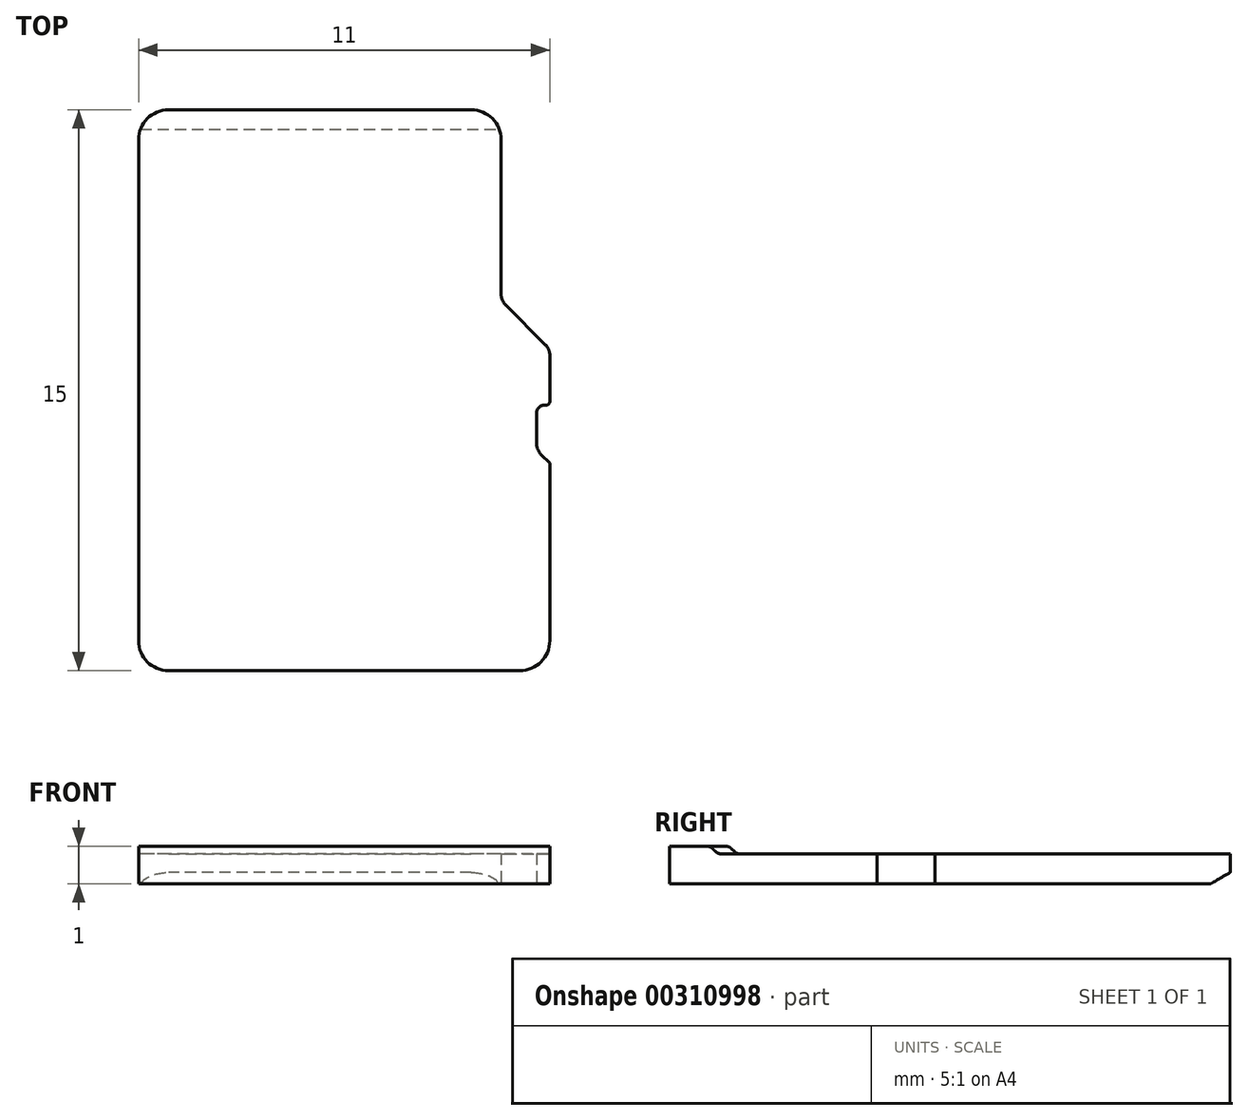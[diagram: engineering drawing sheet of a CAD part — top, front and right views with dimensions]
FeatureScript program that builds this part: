
annotation { "Feature Type Name" : "Feature", "Feature Type Description" : "" }
export const myFeature = defineFeature(function(context is Context, id is Id, definition is map)
    precondition{}
    {
        {
            var Q0;
            Q0=qCreatedBy(makeId("Top.planeOp"),FACE);
            var sketch = newSketch(context, id + "F0", { "sketchPlane" : qUnion([Q0])});
            skLineSegment(sketch, "E0.bottom", {"start": v(-0.8, 0) * mm, "end": v(-10.2, 0) * mm});
            skLineSegment(sketch, "E0.top", {"start": v(0, 15) * mm, "end": v(-11, 15) * mm, "construction": true});
            skLineSegment(sketch, "E0.left", {"start": v(0, 0) * mm, "end": v(0, 5.55) * mm, "construction": true});
            skLineSegment(sketch, "E0.right", {"start": v(-11, 0.8) * mm, "end": v(-11, 14.2) * mm});
            skLineSegment(sketch, "E1", {"start": v(-1.3, 14.2) * mm, "end": v(-1.3, 10.07) * mm});
            skLineSegment(sketch, "E2", {"start": v(-1.18, 9.78) * mm, "end": v(-0.12, 8.72) * mm});
            skLineSegment(sketch, "E3", {"start": v(-10.2, 15) * mm, "end": v(-2.1, 15) * mm});
            skLineSegment(sketch, "E4", {"start": v(0, 8.43) * mm, "end": v(0, 7.2) * mm});
            skPoint(sketch, "E5.visualSharp", {"position": v(-1.3, 15) * mm});
            skArc(sketch, "E5.filletArc", {"start": v(-1.3, 14.2) * mm, "mid": v(-1.53, 14.77) * mm, "end": v(-2.1, 15) * mm});
            skPoint(sketch, "E6.visualSharp", {"position": v(-11, 15) * mm});
            skArc(sketch, "E6.filletArc", {"start": v(-10.2, 15) * mm, "mid": v(-10.77, 14.77) * mm, "end": v(-11, 14.2) * mm});
            skPoint(sketch, "E7.visualSharp", {"position": v(-11, 0) * mm});
            skArc(sketch, "E7.filletArc", {"start": v(-11, 0.8) * mm, "mid": v(-10.77, 0.23) * mm, "end": v(-10.2, 0) * mm});
            skPoint(sketch, "E8.visualSharp", {"position": v(0, 0) * mm});
            skArc(sketch, "E8.filletArc", {"start": v(-0.8, 0) * mm, "mid": v(-0.23, 0.23) * mm, "end": v(0, 0.8) * mm});
            skPoint(sketch, "E9.visualSharp", {"position": v(-1.3, 9.9) * mm});
            skArc(sketch, "E9.filletArc", {"start": v(-1.3, 10.07) * mm, "mid": v(-1.27, 9.91) * mm, "end": v(-1.18, 9.78) * mm});
            skArc(sketch, "E10", {"start": v(0, 1.33) * mm, "mid": v(-5.5, 1.84) * mm, "end": v(-11, 1.33) * mm});
            skArc(sketch, "E11", {"start": v(0, 1) * mm, "mid": v(-5.5, 1.5) * mm, "end": v(-11, 1) * mm});
            skLineSegment(sketch, "E12", {"start": v(-0.1, 7.1) * mm, "end": v(-0.15, 7.1) * mm});
            skLineSegment(sketch, "E13", {"start": v(-0.35, 6.9) * mm, "end": v(-0.35, 6.07) * mm});
            skLineSegment(sketch, "E14", {"start": v(-0.23, 5.78) * mm, "end": v(0, 5.55) * mm});
            skLineSegment(sketch, "E15.trimOffspring", {"start": v(0, 7.1) * mm, "end": v(0, 15) * mm, "construction": true});
            skLineSegment(sketch, "E16.trimOffspring", {"start": v(0, 5.55) * mm, "end": v(0, 0.8) * mm});
            skPoint(sketch, "E17.visualSharp", {"position": v(-0.35, 5.9) * mm});
            skArc(sketch, "E17.filletArc", {"start": v(-0.35, 6.07) * mm, "mid": v(-0.32, 5.91) * mm, "end": v(-0.23, 5.78) * mm});
            skPoint(sketch, "E18.visualSharp", {"position": v(-0.35, 7.1) * mm});
            skArc(sketch, "E18.filletArc", {"start": v(-0.15, 7.1) * mm, "mid": v(-0.3, 7.04) * mm, "end": v(-0.35, 6.9) * mm});
            skPoint(sketch, "E19.visualSharp", {"position": v(0, 7.1) * mm});
            skArc(sketch, "E19.filletArc", {"start": v(-0.1, 7.1) * mm, "mid": v(-0.03, 7.13) * mm, "end": v(0, 7.2) * mm});
            skPoint(sketch, "E20.visualSharp", {"position": v(0, 8.6) * mm});
            skArc(sketch, "E20.filletArc", {"start": v(0, 8.43) * mm, "mid": v(-0.03, 8.59) * mm, "end": v(-0.12, 8.72) * mm});
            skSolve(sketch);
        }
        {
            var Q0;
            Q0=qSketchRegion(id+"F0",true);
            extrude(context, id + "F1", {"entities" : qUnion([Q0]), "depth" : .8 * mm});
        }
        {
            var Q0;
            Q0=makeQuery(id+"F0.imprint","IMPRINT",FACE,{"disambiguationData":[TD([[makeQuery(id+"F0.imprint","IMPRINT",EDGE,{"derivedFrom":sQuery(id+"F0.wireOp",EDGE,"E0.bottom")}),-1.0]])]});
            extrude(context, id + "F2", {"entities" : qUnion([Q0]), "operationType" : NewBodyOperationType.ADD, "depth" : 1 * mm});
        }
        {
            var Q0;
            Q0=makeQuery(id+"F2.boolean.opBoolean","INTERSECT",EDGE,{"derivedFrom":[makeQuery(id+"F1.opExtrude","CAP_FACE",FACE,{"disambiguationData":[OSD([sQuery(id+"F0.wireOp",EDGE,"E0.bottom"),sQuery(id+"F0.wireOp",EDGE,"E0.right"),sQuery(id+"F0.wireOp",EDGE,"E1"),sQuery(id+"F0.wireOp",EDGE,"E2"),sQuery(id+"F0.wireOp",EDGE,"E3"),sQuery(id+"F0.wireOp",EDGE,"E4"),sQuery(id+"F0.wireOp",EDGE,"E5.filletArc"),sQuery(id+"F0.wireOp",EDGE,"E6.filletArc"),sQuery(id+"F0.wireOp",EDGE,"E7.filletArc"),sQuery(id+"F0.wireOp",EDGE,"E8.filletArc"),sQuery(id+"F0.wireOp",EDGE,"E9.filletArc"),sQuery(id+"F0.wireOp",EDGE,"E12"),sQuery(id+"F0.wireOp",EDGE,"E13"),sQuery(id+"F0.wireOp",EDGE,"E14"),sQuery(id+"F0.wireOp",EDGE,"E16.trimOffspring"),sQuery(id+"F0.wireOp",EDGE,"E17.filletArc"),sQuery(id+"F0.wireOp",EDGE,"E18.filletArc"),sQuery(id+"F0.wireOp",EDGE,"E19.filletArc"),sQuery(id+"F0.wireOp",EDGE,"E20.filletArc")])],"isStart":false}),makeQuery(id+"F2.opExtrude","SWEPT_FACE",FACE,{"disambiguationData":[OSD([sQuery(id+"F0.wireOp",EDGE,"E11")])]})]});
            chamfer(context, id + "F3", {"entities" : qUnion([Q0]), "width" : .3 * mm, "tangentPropagation" : true});
        }
        {
            var Q0;
            {var subQ0=makeQuery(id+"F1.opExtrude","CAP_FACE",FACE,{"disambiguationData":[OSD([sQuery(id+"F0.wireOp",EDGE,"E0.bottom"),sQuery(id+"F0.wireOp",EDGE,"E0.right"),sQuery(id+"F0.wireOp",EDGE,"E1"),sQuery(id+"F0.wireOp",EDGE,"E2"),sQuery(id+"F0.wireOp",EDGE,"E3"),sQuery(id+"F0.wireOp",EDGE,"E4"),sQuery(id+"F0.wireOp",EDGE,"E5.filletArc"),sQuery(id+"F0.wireOp",EDGE,"E6.filletArc"),sQuery(id+"F0.wireOp",EDGE,"E7.filletArc"),sQuery(id+"F0.wireOp",EDGE,"E8.filletArc"),sQuery(id+"F0.wireOp",EDGE,"E9.filletArc"),sQuery(id+"F0.wireOp",EDGE,"E12"),sQuery(id+"F0.wireOp",EDGE,"E13"),sQuery(id+"F0.wireOp",EDGE,"E14"),sQuery(id+"F0.wireOp",EDGE,"E16.trimOffspring"),sQuery(id+"F0.wireOp",EDGE,"E17.filletArc"),sQuery(id+"F0.wireOp",EDGE,"E18.filletArc"),sQuery(id+"F0.wireOp",EDGE,"E19.filletArc"),sQuery(id+"F0.wireOp",EDGE,"E20.filletArc")])],"isStart":false});Q0=makeQuery(id+"F3.opChamfer","BLEND_EDGE",EDGE,{"blendedFrom":[makeQuery(id+"F2.boolean.opBoolean","INTERSECT",EDGE,{"derivedFrom":[subQ0,makeQuery(id+"F2.opExtrude","SWEPT_FACE",FACE,{"disambiguationData":[OSD([sQuery(id+"F0.wireOp",EDGE,"E11")])]})]}),subQ0],"blendedInto":[subQ0]});}
            var Q1;
            {var subQ0=sQuery(id+"F0.wireOp",EDGE,"E16.trimOffspring");var subQ1=sQuery(id+"F0.wireOp",EDGE,"E11");var subQ2=sQuery(id+"F0.wireOp",EDGE,"E8.filletArc");var subQ3=sQuery(id+"F0.wireOp",EDGE,"E7.filletArc");var subQ4=sQuery(id+"F0.wireOp",EDGE,"E0.right");var subQ5=sQuery(id+"F0.wireOp",EDGE,"E0.bottom");Q1=makeQuery(id+"F3.opChamfer","BLEND_EDGE",EDGE,{"blendedFrom":[makeQuery(id+"F2.boolean.opBoolean","INTERSECT",EDGE,{"derivedFrom":[makeQuery(id+"F1.opExtrude","CAP_FACE",FACE,{"disambiguationData":[OSD([subQ5,subQ4,sQuery(id+"F0.wireOp",EDGE,"E1"),sQuery(id+"F0.wireOp",EDGE,"E2"),sQuery(id+"F0.wireOp",EDGE,"E3"),sQuery(id+"F0.wireOp",EDGE,"E4"),sQuery(id+"F0.wireOp",EDGE,"E5.filletArc"),sQuery(id+"F0.wireOp",EDGE,"E6.filletArc"),subQ3,subQ2,sQuery(id+"F0.wireOp",EDGE,"E9.filletArc"),sQuery(id+"F0.wireOp",EDGE,"E12"),sQuery(id+"F0.wireOp",EDGE,"E13"),sQuery(id+"F0.wireOp",EDGE,"E14"),subQ0,sQuery(id+"F0.wireOp",EDGE,"E17.filletArc"),sQuery(id+"F0.wireOp",EDGE,"E18.filletArc"),sQuery(id+"F0.wireOp",EDGE,"E19.filletArc"),sQuery(id+"F0.wireOp",EDGE,"E20.filletArc")])],"isStart":false}),makeQuery(id+"F2.opExtrude","SWEPT_FACE",FACE,{"disambiguationData":[OSD([subQ1])]})]}),makeQuery(id+"F2.opExtrude","CAP_FACE",FACE,{"disambiguationData":[OSD([subQ5,subQ4,subQ3,subQ2,subQ1,subQ0])],"isStart":false})],"blendedInto":[makeQuery(id+"F2.opExtrude","CAP_FACE",FACE,{"disambiguationData":[OSD([subQ5,subQ4,subQ3,subQ2,subQ1,subQ0])],"isStart":false})]});}
            fillet(context, id + "F4", {"entities" : qUnion([Q0, Q1]), "radius" : .2 * mm, "tangentPropagation" : true, "allowEdgeOverflow" : false});
        }
        {
            var Q0;
            Q0=makeQuery(id+"F1.opExtrude","CAP_EDGE",EDGE,{"disambiguationData":[OSD([sQuery(id+"F0.wireOp",EDGE,"E3")])],"isStart":true});
            chamfer(context, id + "F5", {"entities" : qUnion([Q0]), "chamferType" : ChamferType.TWO_OFFSETS, "width1" : .52 * mm, "oppositeDirection" : false, "width2" : .3 * mm});
        }
    });
